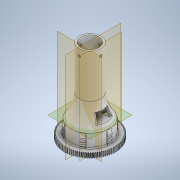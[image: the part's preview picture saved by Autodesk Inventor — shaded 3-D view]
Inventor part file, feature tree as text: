
AUTODESK INVENTOR PART (.ipt)
format: ipt  version: 2022.3 (Build 263350000, 350)  size: 3,567,616 bytes
history: native  units: mm
features: revolve x12, sketch x9, extrude x7, plane x4, hole x3, pattern_circular x2, mirror x2, other x2, fillet x1, projected_geometry x1, reference x1
ambient origin geometry x8: Origin, YZ Plane, XZ Plane, XY Plane, X Axis, Y Axis, Z Axis, Center Point
bodies: Solid1 (feature_tree)
feature tree (44):
  extrude  "Extrusion1"  Depth=4.0mm
  sketch  "Sketch2"  dims[d2=40.0mm d3=0.0mm d4=88.0mm]
  revolve  "Revolution1"  [1 undecoded]
  plane  "Work Plane1"
  extrude  "Extrusion2"  Depth=100.0mm
  sketch  "Sketch18"  dims[d5=50.0mm d8=100.0mm]
  extrude  "Extrusion11"  Depth=100.0mm
  extrude  "Extrusion12"  Depth=100.0mm
  extrude  "Extrusion13"  [1 undecoded]
  pattern_circular  "Circular Pattern2"  [2 undecoded]
  revolve  "Revolution4"  [1 undecoded]
  plane  "Work Plane3"
  plane  "Work Plane4"
  hole  "Hole5"  [1 undecoded]
  hole  "Hole6"  [1 undecoded]
  mirror  "Mirror1"
  mirror  "Mirror2"
  extrude  "Extrusion14"  TaperAngle=0.0deg  [1 undecoded]
  fillet  "Fillet4"  Radius=4.0mm
  extrude  "Extrusion15"  Depth=10.0mm
  plane  "Work Plane5"
  sketch  "Sketch24"  dims[d17=75.0mm d18=5.0mm d19=15.0mm d20=5.2mm d21=5.0mm d22=0.0mm d79=0.0mm d106=4.0mm d107=10.0mm d108=30.0mm d109=0.0mm d110=10.0mm d111=30.0mm d112=0.0mm d113=1.0mm d114=10.0mm d115=1.0mm d116=3.0mm d117=1.0mm d118=5.0mm d119=1.0mm d120=4.0mm d121=1.0mm d122=5.0mm d123=10.0mm d124=90.0deg d131=10.0mm d132=0.0mm d133=1.0mm d134=3.0mm d135=60.0mm d136=360.0deg d138=2.0mm d139=5.0mm d140=2.0mm d141=5.0mm d142=90.0deg d143=25.0mm d144=25.0mm d145=30.0mm d146=3.4mm d147=6.0mm d148=5.9mm d149=2.0mm d150=90.0deg d151=4.2mm d152=0.0mm d153=30.0mm d154=180.0deg d155=3.4mm d156=6.0mm d157=5.9mm d158=2.0mm d159=90.0deg d160=4.2mm d161=0.0mm d162=10.0mm d163=0.0mm d164=2.27mm d165=4.0mm d166=10.0mm d167=0.0mm d168=6.6mm d179=210.0deg d180=150.0deg d181=10.0mm d182=10.0mm d183=90.0deg d184=5.0mm d185=2.0mm d186=2.2mm d187=6.0mm d188=3.1mm d189=4.1mm d190=90.0deg d191=0.9mm d192=0.0mm d193=20.0mm d194=90.0deg d196=20.0mm d197=20.0mm d198=15.0mm d199=10.0mm d200=120.0deg d201=60.0deg d202=10.0mm d203=10.0mm d204=10.0mm d205=1.0mm d206=5.0mm d207=2.0mm d208=5.0mm d209=1.0mm d210=210.0deg d211=35.77925mm d212=27.052603mm d213=20.071286mm d214=11.34464mm d125=0.872665mm d126=0.872665mm d137=14.3117mm]
  revolve  "Revolution5"  [1 undecoded]
  revolve  "Revolution6"  [1 undecoded]
  revolve  "Revolution7"  [1 undecoded]
  hole  "Hole8"  [1 undecoded]
  pattern_circular  "Circular Pattern4"  [2 undecoded]
  revolve  "Revolution8"  [1 undecoded]
  revolve  "Revolution9"  [1 undecoded]
  revolve  "Revolution10"  [1 undecoded]
  revolve  "Revolution11"  [1 undecoded]
  revolve  "Revolution12"  [1 undecoded]
  revolve  "Revolution13"  [1 undecoded]
  revolve  "Revolution14"  [1 undecoded]
  sketch  "Sketch1"  dims[d0=80.0mm d1=4.0mm]
  sketch  "Sketch19"  dims[d9=25.0mm d10=100.0mm]
  sketch  "Sketch20"  dims[d11=4.0mm d12=100.0mm]
  sketch  "Sketch21"  dims[d13=360.0deg d14=-45.0mm]
  sketch  "Sketch22"  dims[d15=5.0mm]
  sketch  "Sketch23"  dims[d16=75.0mm]
  projected_geometry  "Projected Loop3"
  reference  "Reference1"
  other  "v3.0.iam"
  other  "Spur Gear (95 teeth):1"
note: 21 required parameter values undecoded (feature->parameter linkage not recoverable at this tier; creation-order binding heuristic only, values carry confidence <= 0.55)